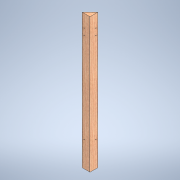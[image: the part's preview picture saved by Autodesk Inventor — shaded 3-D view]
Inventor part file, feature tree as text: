
AUTODESK INVENTOR PART (.ipt)
format: ipt  version: 2022 (Build 260153000, 153)  size: 126,976 bytes
history: native  units: mm
features: sketch x4, hole x3, other x1, extrude x1
ambient origin geometry x8: Origin, YZ Plane, XZ Plane, XY Plane, X Axis, Y Axis, Z Axis, Center Point
bodies: Body1 (feature_tree)
feature tree (9):
  other  "Sólido1"
  extrude  "Extrusão1"  Depth=700.0mm
  hole  "Furo1"  [1 undecoded]
  hole  "Furo2"  [1 undecoded]
  hole  "Furo3"  [1 undecoded]
  sketch  "Esboço1"  dims[d2=700.0mm d3=0.0mm d4=100.0mm]
  sketch  "Esboço2"  dims[d5=21.5mm d6=21.5mm]
  sketch  "Esboço3"  dims[d7=3.0mm d8=6.0mm d9=4.0mm d10=2.0mm d11=90.0deg d12=8.0mm d13=20.594885mm d14=468.0mm]
  sketch  "Esboço4"  dims[d15=468.0mm d16=3.0mm d17=6.0mm d18=4.0mm d19=2.0mm d20=90.0deg d21=8.0mm d22=20.594885mm d23=33.0mm d24=3.0mm d25=6.0mm d26=4.0mm d27=2.0mm d28=90.0deg d29=8.0mm d30=20.594885mm]
note: 3 required parameter values undecoded (feature->parameter linkage not recoverable at this tier; creation-order binding heuristic only, values carry confidence <= 0.55)
